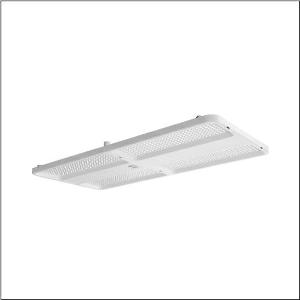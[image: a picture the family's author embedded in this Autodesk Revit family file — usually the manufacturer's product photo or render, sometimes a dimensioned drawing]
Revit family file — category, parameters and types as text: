
# Revit family: highbay_21_maxi_52hn11db4mda03
name_source: partatom
category: Lighting Fixtures
units: mm (PartAtom-declared; Revit-internal decimal feet)

## family parameters
Cut with Voids When Loaded = No
Host = Face
Light Source = No
Part Type = Normal
Room Calculation Point = No
Round Connector Dimension = Use Diameter
Shared = No

## types (1)
- --- (1 x LED, 28000 lm, 144 W, 4000K)
    Apparent Load = 144 VA
    CIE Flux Codes = 89 97 99 100 100
    Color Rendering = 80
    Color Temperature = 4000K
    Default Elevation = 1800 mm
    Description = high bay luminaire Highbay 21 maxi; direct symmetric narrow distribution, light control with lens of PMMA; UGR ≤ 19 (X = 4H | Y = 8H | S = 0.25H | reflection values 70/50/20); luminous flux: 28.000lm; light colour: 840, colour temperature: 4000K, MacAdam ≤ 3 SDCM (initial), colour rendering: CRI > 80; luminous efficacy: 194,4lm/W; rated service life: 75.000h (L80) at AT= ta max; control: DALI 2; for wired networking: open and standardized DALI2 interface enables full flexibility and future-proofing for changes in use or functional adaptation through individual programming; multi-sensor luminaire consisting of a DALI2 multi-sensor and DALI2 ECG; multi-sensor luminaire for wired connection to a DALI2 application controller (e.g., SITECO Connect 11 or 21); can also be connected to existing on-site lighting or building automation systems upon request; integrated DALI2 sensor certified according to IEC 62386, Parts 101, 103, 303, and 304; integrated DALI2 ECG provides luminaire data (according to IEC 62386, Part 251), energy data (Part 252), and monitoring and analytics data (Part 253) to higher-level systems for further processing; luminaire with PIR sensor (passive-infrared); with light sensor; luminaire connection: terminal, 5-pole, max. 2.5mm² (cable entry for one cable, Ø 8.5..16mm); mains connection: 230..240V, AC 50/60Hz; connected load: 144W; protection rating (complete): IP65; insulation class (complete): insulation class I (protective earthing); protection symbol: D; certification: CE, UKCA; internal wiring halogen-free; luminaire LABS conformity tested according to VDMA 24364:2018-05; Suitable for use in the food industry according to the specifications of IFS-Food, HACCP and/or BRC; housing frame of high-performance plastic PA6, matt traffic white (RAL 9016); cover of PMMA; dimension (LxWxH): 946 x 442 x 72mm; permissible operating ambient temperature: -20..+45°C (reducing of maximum allowable ambient temperature of 5°C with ceiling mounting); packaging unit: 1 piece; (delivery without accessories; please order mounting accessories separately)
    Height = 72 mm  [stored 0.23622 ft]
    Lamp = 1 x LED
    Lamp Light Flux = 28000 lm
    Lamp Power = 144 W
    Lamp count = 1
    Length = 946 mm
    Luminous efficacy = 194 lm/W
    Manufacturer = Siteco
    ModVariant = No
    Model = 52HN11DB4MDA03
    Mounting Place = Ceiling
    Mounting Type = Pendant
    Number of Poles = 1
    OnlyDefault = Yes
    Power Factor = 1
    Product Name = Highbay 21 maxi
    Product group = high bay luminaire
    ProductGroupID = 902
    Protection Class = Protection class I
    Protection Degree = IP 65
    RLX_Detail_Level = 1
    RLX_Emergency_Light_Flux = 0 lm
    RLX_Emergency_Type = 0
    RLX_Emergency_Type_DB = No
    RlxData = <blob elided: 128281 chars, md5=0f3dfd3b>
    Socket = socket
    Standby Power = 0 W
    System Light Flux = 27999 lm
    System Power = 144 W
    Type Comments = factory setting: luminous flux: 100 % | dim-lin: 254 | 668 mA
    Type Image = l_1363267.jpg
    URL = http://relux.com
    VarID = @adj_012281
    Voltage = 0 V
    Weight = 0.00 kg
    Width = 442 mm

note: [stored X ft] marks values corroborated as IEEE doubles in the binary element streams (Revit-internal decimal feet)

## geometry (parser evidence)
native form markers: Blend x4, Sweep x9
no freeform markers — native parametric forms only
